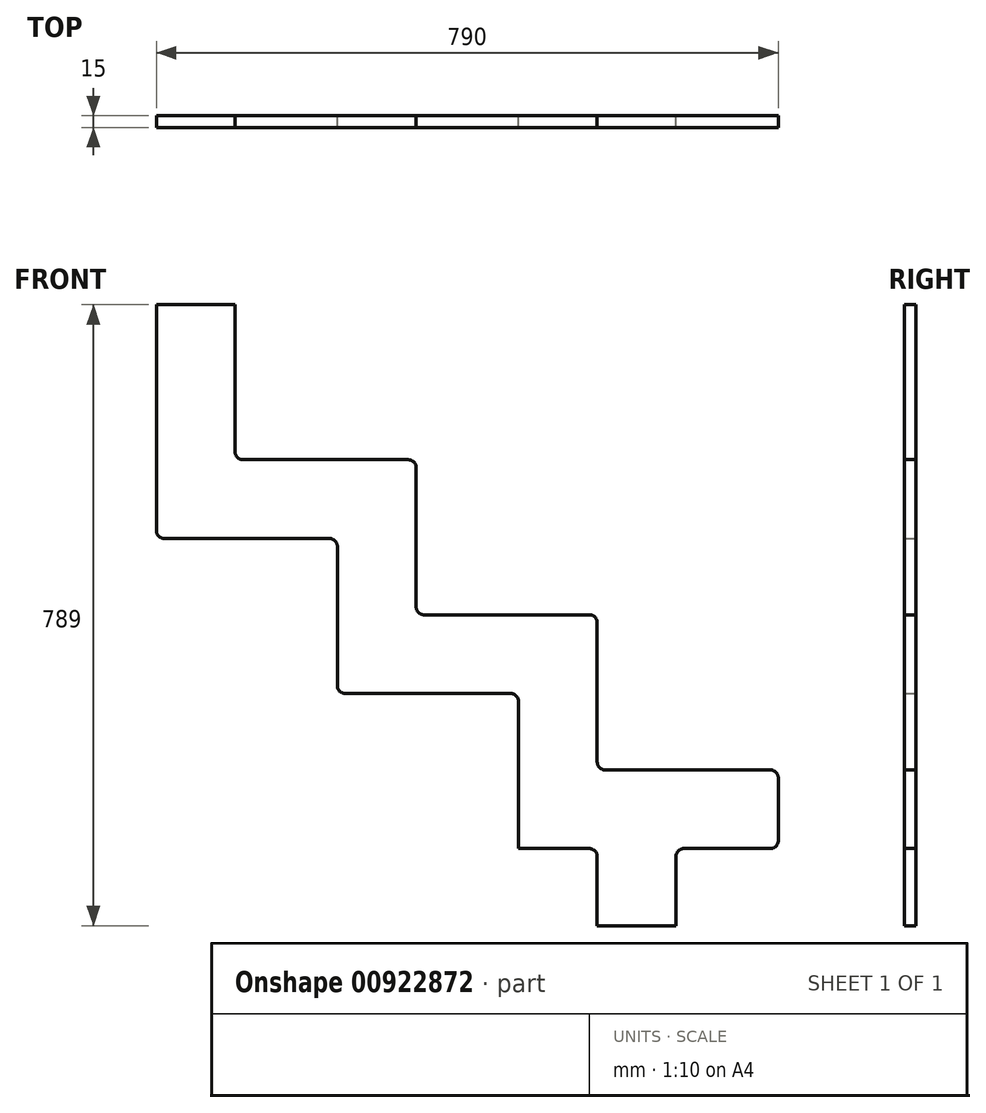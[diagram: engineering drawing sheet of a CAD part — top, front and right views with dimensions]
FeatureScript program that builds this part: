
annotation { "Feature Type Name" : "Feature", "Feature Type Description" : "" }
export const myFeature = defineFeature(function(context is Context, id is Id, definition is map)
    precondition{}
    {
        {
            var Q0;
            Q0=qCreatedBy(makeId("Front.planeOp"),FACE);
            var sketch = newSketch(context, id + "F0", { "sketchPlane" : qUnion([Q0])});
            skLineSegment(sketch, "E0", {"start": v(100, 100) * mm, "end": v(0, 100) * mm});
            skLineSegment(sketch, "E1", {"start": v(0, 100) * mm, "end": v(0, -187) * mm});
            skLineSegment(sketch, "E2", {"start": v(100, 100) * mm, "end": v(100, -87) * mm});
            skLineSegment(sketch, "E3", {"start": v(110, -97) * mm, "end": v(320, -97) * mm});
            skLineSegment(sketch, "E4", {"start": v(330, -107) * mm, "end": v(330, -284) * mm});
            skLineSegment(sketch, "E5", {"start": v(340, -294) * mm, "end": v(550, -294) * mm});
            skLineSegment(sketch, "E6", {"start": v(560, -304) * mm, "end": v(560, -481) * mm});
            skLineSegment(sketch, "E7", {"start": v(570, -491) * mm, "end": v(780, -491) * mm});
            skLineSegment(sketch, "E8", {"start": v(550, -591) * mm, "end": v(460, -591) * mm});
            skLineSegment(sketch, "E9", {"start": v(460, -591) * mm, "end": v(460, -404) * mm});
            skLineSegment(sketch, "E10", {"start": v(450, -394) * mm, "end": v(240, -394) * mm});
            skLineSegment(sketch, "E11", {"start": v(230, -384) * mm, "end": v(230, -207) * mm});
            skLineSegment(sketch, "E12", {"start": v(560, -601) * mm, "end": v(560, -689) * mm});
            skLineSegment(sketch, "E13", {"start": v(560, -689) * mm, "end": v(660, -689) * mm});
            skLineSegment(sketch, "E14", {"start": v(660, -689) * mm, "end": v(660, -601) * mm});
            skLineSegment(sketch, "E15", {"start": v(670, -591) * mm, "end": v(780, -591) * mm});
            skLineSegment(sketch, "E16", {"start": v(790, -581) * mm, "end": v(790, -501) * mm});
            skLineSegment(sketch, "E17", {"start": v(560, -294) * mm, "end": v(790, -491) * mm, "construction": true});
            skLineSegment(sketch, "E18", {"start": v(10, -197) * mm, "end": v(220, -197) * mm});
            skPoint(sketch, "E19.visualSharp", {"position": v(100, -97) * mm});
            skArc(sketch, "E19.filletArc", {"start": v(100, -87) * mm, "mid": v(102.93, -94.07) * mm, "end": v(110, -97) * mm});
            skPoint(sketch, "E20.visualSharp", {"position": v(0, -197) * mm});
            skArc(sketch, "E20.filletArc", {"start": v(0, -187) * mm, "mid": v(2.93, -194.07) * mm, "end": v(10, -197) * mm});
            skPoint(sketch, "E21.visualSharp", {"position": v(230, -197) * mm});
            skArc(sketch, "E21.filletArc", {"start": v(230, -207) * mm, "mid": v(227.07, -199.93) * mm, "end": v(220, -197) * mm});
            skPoint(sketch, "E22.visualSharp", {"position": v(330, -97) * mm});
            skArc(sketch, "E22.filletArc", {"start": v(330, -107) * mm, "mid": v(327.07, -99.93) * mm, "end": v(320, -97) * mm});
            skPoint(sketch, "E23.visualSharp", {"position": v(330, -294) * mm});
            skArc(sketch, "E23.filletArc", {"start": v(330, -284) * mm, "mid": v(332.93, -291.07) * mm, "end": v(340, -294) * mm});
            skPoint(sketch, "E24.visualSharp", {"position": v(230, -394) * mm});
            skArc(sketch, "E24.filletArc", {"start": v(230, -384) * mm, "mid": v(232.93, -391.07) * mm, "end": v(240, -394) * mm});
            skPoint(sketch, "E25.visualSharp", {"position": v(560, -294) * mm});
            skArc(sketch, "E25.filletArc", {"start": v(560, -304) * mm, "mid": v(557.07, -296.93) * mm, "end": v(550, -294) * mm});
            skPoint(sketch, "E26.visualSharp", {"position": v(460, -394) * mm});
            skArc(sketch, "E26.filletArc", {"start": v(460, -404) * mm, "mid": v(457.07, -396.93) * mm, "end": v(450, -394) * mm});
            skPoint(sketch, "E27.visualSharp", {"position": v(560, -491) * mm});
            skArc(sketch, "E27.filletArc", {"start": v(560, -481) * mm, "mid": v(562.93, -488.07) * mm, "end": v(570, -491) * mm});
            skPoint(sketch, "E28.visualSharp", {"position": v(790, -491) * mm});
            skArc(sketch, "E28.filletArc", {"start": v(790, -501) * mm, "mid": v(787.07, -493.93) * mm, "end": v(780, -491) * mm});
            skPoint(sketch, "E29.visualSharp", {"position": v(790, -591) * mm});
            skArc(sketch, "E29.filletArc", {"start": v(780, -591) * mm, "mid": v(787.07, -588.07) * mm, "end": v(790, -581) * mm});
            skPoint(sketch, "E30.visualSharp", {"position": v(660, -591) * mm});
            skArc(sketch, "E30.filletArc", {"start": v(670, -591) * mm, "mid": v(662.93, -593.93) * mm, "end": v(660, -601) * mm});
            skPoint(sketch, "E31.visualSharp", {"position": v(660, -689) * mm});
            skLineSegment(sketch, "E31.filletArc", {"start": v(660, -689) * mm, "end": v(660, -689) * mm});
            skPoint(sketch, "E32.visualSharp", {"position": v(560, -689) * mm});
            skLineSegment(sketch, "E32.filletArc", {"start": v(560, -689) * mm, "end": v(560, -689) * mm});
            skPoint(sketch, "E33.visualSharp", {"position": v(560, -591) * mm});
            skArc(sketch, "E33.filletArc", {"start": v(560, -601) * mm, "mid": v(557.07, -593.93) * mm, "end": v(550, -591) * mm});
            skSolve(sketch);
        }
        {
            var Q0;
            Q0 = qSketchRegion(id + "F0", true);
            extrude(context, id + "F1", {"entities" : qUnion([Q0]), "depth" : 15 * mm, "offsetDistance" : 25 * mm});
        }
    });
